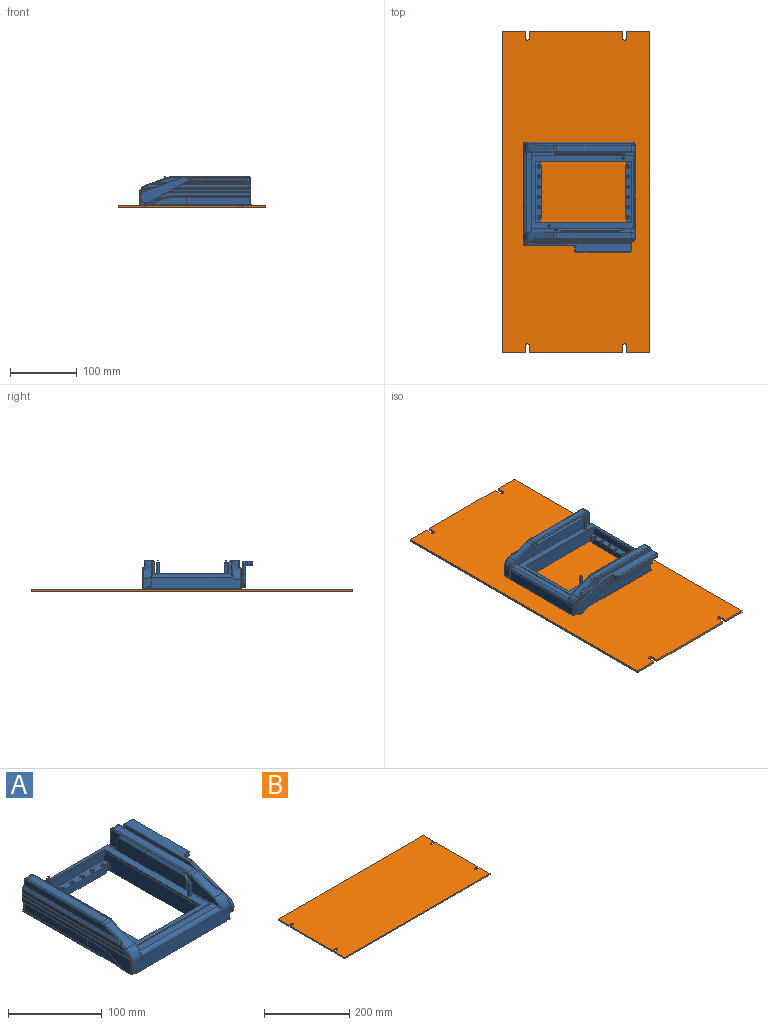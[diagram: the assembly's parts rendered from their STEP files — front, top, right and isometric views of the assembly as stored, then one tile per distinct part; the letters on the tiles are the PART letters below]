
ASSEMBLY  parts=2 mates=1
PART A: 333 faces, bbox 167.3x170.3x45.8 mm
  f0: plane 100.6x2.54mm, normal (0.71,0,0.71), area 346.7mm2, adj f1,f2,f3,f7
  f1: cylinder r=9.65mm len=9.65mm, axis (-1,0,0), area 36.1mm2, adj f0,f3,f4,f6,f7
  f2: cylinder r=9.65mm len=9.65mm, axis (1,0,0), area 36.1mm2, adj f0,f3,f5,f6,f7
  f3: plane 87.55x0.64mm, normal (0,0,1), area 55.6mm2, adj f0,f1,f2,f6
  f4: plane 11.86x3.18mm, normal (0,-1,0), area 37.7mm2, adj f1,f6,f7,f8
  f5: plane 11.86x3.18mm, normal (0,1,0), area 37.7mm2, adj f2,f6,f7,f8
  f6: plane 106.85x21.51mm, normal (-1,0,0), area 2258.8mm2, adj f1,f2,f3,f4,f5,f8
  f7: plane 106.85x18.97mm, normal (1,0,0), area 2013.7mm2, adj f0,f1,f2,f4,f5,f8
  f8: plane 154.94x122.53mm, normal (0,0,1), area 856.5mm2, adj f4,f5,f6,f7,f9,f10,f11,f12
  f9: plane 106.85x18.97mm, normal (-1,0,0), area 2013.7mm2, adj f8,f10,f12,f24,f25,f26
  f10: plane 11.86x3.18mm, normal (0,1,0), area 37.7mm2, adj f8,f9,f11,f26
  f11: plane 106.85x21.51mm, normal (1,0,0), area 2258.8mm2, adj f8,f10,f12,f24,f26,f27
  f12: plane 11.86x3.18mm, normal (0,-1,0), area 37.7mm2, adj f8,f9,f11,f24
  f13: plane 109.73x2.36mm, normal (0,-1,0), area 259.2mm2, adj f8,f14,f16,f28
  f14: plane 153.16x2.36mm, normal (-1,0,0), area 361.8mm2, adj f8,f13,f15,f28
  f15: plane 109.73x2.36mm, normal (0,1,0), area 259.2mm2, adj f8,f14,f16,f28
  f16: plane 153.16x2.36mm, normal (1,0,0), area 361.8mm2, adj f8,f13,f15,f28
  f17: plane 162.68x20.83mm, normal (-1,0,0), area 3006.5mm2, adj f8,f18,f23,f29,f30,f31,f32,f33
  f18: cylinder r=1.52mm len=17.53mm, axis (0,0,-1), area 38.5mm2, adj f8,f17,f34,f36,f37,f38,f39,f45
  f19: plane 167.66x18.05mm, normal (-1,0,0), area 53.8mm2, adj f8,f20,f43,f45,f46,f47,f48,f49
  f20: cylinder r=0.51mm len=12.68mm, axis (1,0.03,0), area 9.3mm2, adj f8,f19,f21,f51,f52,f53
  f21: cylinder r=1.52mm len=17.86mm, axis (0,0,-1), area 41.1mm2, adj f8,f20,f22,f53,f54,f55,f56,f57
  f22: plane 162.82x21.1mm, normal (1,0,0), area 3049.8mm2, adj f8,f21,f23,f29,f35,f60,f61,f62
  f23: plane 118.36x1.27mm, normal (0,1,0), area 150.3mm2, adj f8,f17,f22,f35
  f24: cylinder r=9.65mm len=9.65mm, axis (-1,0,0), area 36.1mm2, adj f9,f11,f12,f25,f27
  f25: plane 100.6x2.54mm, normal (-0.71,0,0.71), area 346.7mm2, adj f9,f24,f26,f27
  f26: cylinder r=9.65mm len=9.65mm, axis (1,0,0), area 36.1mm2, adj f9,f10,f11,f25,f27
  f27: plane 87.55x0.64mm, normal (0,0,1), area 55.6mm2, adj f11,f24,f25,f26
  f28: plane 153.16x109.73mm, normal (0,0,1), area 3395.6mm2, adj f13,f14,f15,f16,f64,f65,f66,f67
  f29: cylinder r=4.83mm len=123.65mm, axis (-1,0,0), area 914.9mm2, adj f17,f22,f30,f35,f63,f68,f69,f70
  f30: torus R=14.35mm, axis (-1,0,0), area 28.9mm2, adj f17,f29,f31,f69
  f31: cylinder r=1.52mm len=35.07mm, axis (0,-0.94,-0.34), area 88mm2, adj f17,f30,f32,f72
  f32: torus R=14.35mm, axis (-1,0,0), area 12.8mm2, adj f17,f31,f33,f73
  f33: cylinder r=1.52mm len=112.51mm, axis (0,1,0), area 269.2mm2, adj f17,f32,f34,f74
  f34: torus R=3.3mm, axis (-1,0,0), area 16mm2, adj f17,f18,f33,f75
  f35: plane 118.36x7.87mm, normal (0,0,1), area 932mm2, adj f17,f22,f23,f29
  f36: plane 12.45x12.07mm, normal (0,1,0), area 125.9mm2, adj f18,f75,f76,f77,f78,f79,f80
  f37: torus R=1.02mm, axis (0,0,-1), area 1mm2, adj f18,f38,f80,f81
  f38: plane 12.87x2.4mm, normal (0,1,0), area 14.6mm2, adj f18,f37,f39,f81,f82,f83
  f39: torus R=1.02mm, axis (0,0,-1), area 1mm2, adj f18,f38,f83,f84
  f40: plane 167.64x0.25mm, normal (1,0,0), area 9.7mm2, adj f41,f45,f87,f88,f89,f105
  f41: plane 165.1x142.24mm, normal (0,0,1), area 1026.7mm2, adj f40,f42,f45,f88,f90,f91,f92
  f42: plane 167.64x2.54mm, normal (-1,0,0), area 66.3mm2, adj f41,f43,f45,f47,f87,f88,f93,f94
  f43: plane 167.64x6.5mm, normal (0,0,1), area 1089.7mm2, adj f19,f42,f45,f95,f105
  f44: plane 2.16x0.76mm, normal (1,0,0), area 1mm2, adj f45,f86,f96,f97,f98,f99
  f45: plane 141.1x23.3mm, normal (0,1,0), area 2728.3mm2, adj f8,f18,f19,f40,f41,f42,f43,f44
  f46: plane 167.49x8.28mm, normal (0.02,0,-1), area 1087.4mm2, adj f19,f47,f93,f95,f104,f105
  f47: plane 18.26x11.1mm, normal (-0.03,1,0), area 145mm2, adj f19,f42,f46,f48,f94,f95,f106,f107
  f48: cylinder r=0.51mm len=11.02mm, axis (-1,-0.03,0), area 8.8mm2, adj f19,f47,f49,f109
  f49: plane 11.64x0.66mm, normal (0,0,1), area 2.9mm2, adj f19,f48,f50,f109
  f50: plane 11.71x1.15mm, normal (-0.03,1,0), area 13.4mm2, adj f19,f49,f51,f52,f109,f110
  f51: plane 11.64x0.66mm, normal (0,0,-1), area 2.9mm2, adj f19,f20,f50,f52
  f52: torus R=1.02mm, axis (0,0,-1), area 1.6mm2, adj f20,f50,f51,f110,f111,f112,f113
  f53: plane 12.07x2.92mm, normal (-0.03,1,0), area 35.3mm2, adj f20,f21,f54,f112
  f54: cylinder r=0.51mm len=13.22mm, axis (-1,-0.03,0), area 10.1mm2, adj f21,f53,f55,f114
  f55: plane 14.06x0.74mm, normal (0,0,1), area 3.5mm2, adj f21,f54,f56,f114
  f56: plane 14.12x1.15mm, normal (-0.03,1,0), area 16.1mm2, adj f21,f55,f57,f114,f115,f116
  f57: plane 14.06x0.74mm, normal (0,0,-1), area 3.5mm2, adj f21,f56,f58,f116
  f58: cylinder r=0.51mm len=13.22mm, axis (1,0.03,0), area 10.1mm2, adj f21,f57,f59,f116
  f59: plane 12.54x12.16mm, normal (-0.03,1,0), area 126mm2, adj f21,f58,f117,f118,f119,f120,f121
  f60: torus R=3.25mm, axis (1,0,0), area 16.3mm2, adj f21,f22,f117,f332
  f61: torus R=14.3mm, axis (1,0,0), area 13.1mm2, adj f22,f62,f123,f332
  f62: cylinder r=1.52mm len=35.07mm, axis (0,0.94,0.34), area 90mm2, adj f22,f61,f63,f124
  f63: torus R=14.3mm, axis (1,0,0), area 32mm2, adj f22,f29,f62,f70
  f64: plane 92.46x2.36mm, normal (0,-1,0), area 218.4mm2, adj f28,f65,f67,f125
  f65: plane 144.78x2.36mm, normal (-1,0,0), area 342mm2, adj f28,f64,f66,f125
  f66: plane 92.46x2.36mm, normal (0,1,0), area 218.4mm2, adj f28,f65,f67,f125
  f67: plane 144.78x2.36mm, normal (1,0,0), area 342mm2, adj f28,f64,f66,f125
  f68: plane 5.42x0.96mm, normal (1,0,0), area 0.8mm2, adj f29,f69,f105
  f69: cylinder r=15.88mm len=14.92mm, axis (-1,0,0), area 227.8mm2, adj f29,f30,f68,f72,f105,f126
  f70: cone r=15.88mm half-angle=2deg, axis (1,0,0), area 227.8mm2, adj f29,f63,f71,f93,f103,f105,f124,f127
  f71: plane 2.49x0.5mm, normal (-1,0,0), area 0.2mm2, adj f29,f70,f105
  f72: plane 34.82x12.85mm, normal (0,-0.34,0.94), area 350.2mm2, adj f31,f69,f73,f128,f129,f130,f131
  f73: cylinder r=15.88mm len=8.89mm, axis (-1,0,0), area 49.3mm2, adj f32,f72,f74,f132
  f74: plane 112.39x8.89mm, normal (0,0,1), area 999.1mm2, adj f33,f73,f75,f133
  f75: cylinder r=4.83mm len=8.89mm, axis (-1,0,0), area 67.4mm2, adj f34,f36,f74,f134
  f76: cylinder r=1.52mm len=5.21mm, axis (0,0,-1), area 12.5mm2, adj f36,f77,f134,f135
  f77: torus R=3.05mm, axis (0,1,0), area 7.8mm2, adj f36,f76,f78,f136
  f78: cylinder r=1.52mm len=1.52mm, axis (1,0,0), area 0.3mm2, adj f36,f77,f137,f138
  f79: cylinder r=1.52mm len=4.19mm, axis (0,0,-1), area 10mm2, adj f36,f137,f139,f140
  f80: cylinder r=0.51mm len=12.07mm, axis (-1,0,0), area 9.6mm2, adj f36,f37,f81,f140
  f81: plane 154.7x13.75mm, normal (0,0,-1), area 41.9mm2, adj f37,f38,f80,f82,f140,f141,f142,f143
  f82: cylinder r=1.52mm len=1.52mm, axis (0,0,1), area 2.7mm2, adj f38,f81,f83,f143
  f83: plane 154.7x13.75mm, normal (0,0,1), area 41.9mm2, adj f38,f39,f82,f84,f142,f143,f144,f145
  f84: cylinder r=0.51mm len=12.07mm, axis (1,0,0), area 9.6mm2, adj f39,f45,f83,f144
  f85: cylinder r=1.52mm len=2.92mm, axis (0,0,-1), area 7mm2, adj f45,f144,f146,f147
  f86: cylinder r=0.51mm len=10.95mm, axis (-1,0,0), area 8.7mm2, adj f44,f45,f96,f147
  f87: plane 136.65x3.3mm, normal (0,0,-1), area 451.2mm2, adj f40,f42,f88,f105
  f88: plane 142.24x1.8mm, normal (0,-1,0), area 228.7mm2, adj f40,f41,f42,f87,f90,f92,f148
  f89: plane 167.67x6mm, normal (0,0,-1), area 590.9mm2, adj f40,f45,f102,f105,f149,f150,f151,f152
  f90: plane 165.1x1.8mm, normal (1,0,0), area 297.2mm2, adj f41,f88,f91,f148
  f91: plane 142.24x1.8mm, normal (0,1,0), area 256.1mm2, adj f41,f90,f92,f148
  f92: plane 165.1x1.8mm, normal (-1,0,0), area 297.2mm2, adj f41,f88,f91,f148
  f93: plane 14.22x12.07mm, normal (-0.03,-1,0), area 155.1mm2, adj f42,f46,f70,f94,f95,f104,f155
  f94: plane 167.04x6mm, normal (0,0,-1), area 587.4mm2, adj f42,f47,f93,f106,f155,f156,f157,f158
  f95: plane 167x0.17mm, normal (1,0,0), area 28.5mm2, adj f43,f46,f47,f93
  f96: plane 157.24x11.96mm, normal (0,0,-1), area 42.1mm2, adj f44,f86,f97,f147,f161,f162,f163,f164
  f97: plane 10.18x1.14mm, normal (0,1,0), area 11.6mm2, adj f44,f96,f98,f164
  f98: plane 154.34x11.96mm, normal (0,0,1), area 42mm2, adj f44,f97,f99,f162,f163,f164,f165,f166
  f99: cylinder r=0.51mm len=10.95mm, axis (1,0,0), area 8.7mm2, adj f44,f45,f98,f166
  f100: cylinder r=1.52mm len=4.19mm, axis (0,0,-1), area 10mm2, adj f45,f149,f166,f167
  f101: torus R=3.05mm, axis (0,1,0), area 7.8mm2, adj f45,f102,f167,f168
  f102: cylinder r=1.52mm len=10.92mm, axis (0,0,-1), area 26.1mm2, adj f45,f89,f101,f151
  f103: torus R=14.3mm, axis (1,0,0), area 0.8mm2, adj f70,f104,f105
  f104: cylinder r=1.52mm len=11.96mm, axis (0,0,-1), area 8.8mm2, adj f46,f93,f103,f105
  f105: plane 141.72x17.64mm, normal (0,-1,0), area 2253.4mm2, adj f19,f29,f40,f42,f43,f46,f68,f69
  f106: cylinder r=1.52mm len=10.92mm, axis (0,0,-1), area 25.6mm2, adj f47,f94,f107,f160
  f107: bspline ~3.05x3.05mm, area 7.7mm2, adj f47,f106,f169,f170
  f108: cylinder r=1.52mm len=4.19mm, axis (0,0,-1), area 9.8mm2, adj f47,f109,f156,f169
  f109: torus R=1.02mm, axis (0,0,-1), area 1.6mm2, adj f48,f49,f50,f108,f110,f171,f172
  f110: plane 143.84x1.15mm, normal (-1,0,0), area 164.4mm2, adj f50,f52,f109,f113,f172,f173
  f111: cylinder r=0.51mm len=162.23mm, axis (0,-1,0), area 128.4mm2, adj f52,f113,f173,f174,f175
  f112: cylinder r=1.52mm len=2.92mm, axis (0,0,-1), area 6.8mm2, adj f52,f53,f114,f175
  f113: plane 156.42x0.25mm, normal (0,0,-1), area 38.6mm2, adj f52,f110,f111,f173
  f114: torus R=1.02mm, axis (0,0,-1), area 1.6mm2, adj f54,f55,f56,f112,f115,f176,f177
  f115: plane 141.3x1.15mm, normal (-1,0,0), area 161.5mm2, adj f56,f114,f116,f177,f178,f179
  f116: torus R=1.02mm, axis (0,0,-1), area 1.6mm2, adj f56,f57,f58,f115,f118,f178,f180
  f117: cone r=4.83mm half-angle=2deg, axis (1,0,0), area 64.5mm2, adj f59,f60,f122,f181
  f118: cylinder r=1.52mm len=4.19mm, axis (0,0,-1), area 9.8mm2, adj f59,f116,f182,f183
  f119: cylinder r=1.52mm len=1.53mm, axis (-1,-0.03,0), area 0.3mm2, adj f59,f120,f183,f184
  f120: bspline ~3.05x3.05mm, area 7.7mm2, adj f59,f119,f121,f185
  f121: cylinder r=1.52mm len=5.21mm, axis (0,0,-1), area 12.2mm2, adj f59,f120,f181,f186
  f122: plane 112.39x8.89mm, normal (-0.03,0,1), area 999.8mm2, adj f117,f123,f187,f332
  f123: cone r=15.88mm half-angle=2deg, axis (1,0,0), area 48.6mm2, adj f61,f122,f124,f188
  f124: plane 34.92x13.24mm, normal (-0.03,-0.34,0.94), area 354mm2, adj f62,f70,f123,f189,f190,f191,f192
  f125: plane 144.78x92.46mm, normal (0,0,1), area 120.3mm2, adj f64,f65,f66,f67,f194,f195,f196,f197
  f126: torus R=14.35mm, axis (1,0,0), area 42.1mm2, adj f69,f128,f139,f142,f146,f149,f150,f162
  f127: torus R=13.88mm, axis (-1,0,0), area 39.3mm2, adj f70,f155,f156,f173,f174,f175,f179,f182
  f128: cylinder r=1.52mm len=5.7mm, axis (0,-0.94,-0.34), area 13.2mm2, adj f72,f126,f139,f206
  f129: cylinder r=1.52mm len=0.52mm, axis (-1,0,0), area 0.1mm2, adj f72,f130,f138,f206
  f130: bspline ~8.9x3.05mm, area 14.3mm2, adj f72,f129,f131,f136
  f131: cylinder r=1.52mm len=21.52mm, axis (0,0.94,0.34), area 53.5mm2, adj f72,f130,f132,f135
  f132: torus R=14.35mm, axis (1,0,0), area 12.8mm2, adj f73,f131,f133,f135
  f133: cylinder r=1.52mm len=112.39mm, axis (0,1,0), area 269mm2, adj f74,f132,f134,f135
  f134: torus R=3.3mm, axis (1,0,0), area 16.1mm2, adj f75,f76,f133,f135
  f135: plane 141.6x8.51mm, normal (1,0,0), area 1102.7mm2, adj f76,f131,f132,f133,f134,f136
  f136: cylinder r=1.52mm len=149.98mm, axis (0,1,0), area 351.7mm2, adj f77,f130,f135,f138
  f137: sphere r=1.52mm, area 2.3mm2, adj f78,f79,f207
  f138: plane 149.98x0.13mm, normal (0,0,1), area 19mm2, adj f78,f129,f136,f207
  f139: plane 159.34x4.27mm, normal (1,0,0), area 650.8mm2, adj f79,f126,f128,f141,f202,f207
  f140: torus R=1.02mm, axis (0,0,-1), area 1.7mm2, adj f79,f80,f81,f141
  f141: cylinder r=0.51mm len=153.69mm, axis (0,-1,0), area 122.6mm2, adj f81,f139,f140,f202
  f142: cylinder r=315.21mm len=20.88mm, axis (0,0,1), area 23.6mm2, adj f81,f83,f126,f143,f145,f199,f202
  f143: plane 140.27x1.14mm, normal (1,0,0), area 160.3mm2, adj f81,f82,f83,f142
  f144: torus R=1.02mm, axis (0,0,-1), area 1.7mm2, adj f83,f84,f85,f145
  f145: cylinder r=0.51mm len=161.4mm, axis (0,1,0), area 127.3mm2, adj f83,f142,f144,f146,f199
  f146: plane 163.23x2.92mm, normal (1,0,0), area 474.4mm2, adj f85,f126,f145,f161
  f147: torus R=1.02mm, axis (0,0,-1), area 1.7mm2, adj f85,f86,f96,f161
  f148: plane 165.1x142.24mm, normal (0,0,-1), area 9069.4mm2, adj f88,f90,f91,f92,f208,f209,f210,f211
  f149: plane 164.6x18.17mm, normal (1,0,0), area 886.7mm2, adj f89,f100,f126,f150,f154,f165,f216,f217
  f150: cylinder r=1.52mm len=14.22mm, axis (0,0,1), area 34mm2, adj f89,f105,f126,f149
  f151: plane 95.57x10.92mm, normal (1,0,0), area 1043.8mm2, adj f89,f102,f152,f168
  f152: cylinder r=508mm len=52.87mm, axis (0,0,-1), area 365mm2, adj f89,f151,f153,f219
  f153: bspline ~40.64x12.99mm, area 59.1mm2, adj f89,f152,f154,f219
  f154: bspline ~40.94x14.48mm, area 72.9mm2, adj f89,f149,f153,f217
  f155: cylinder r=1.52mm len=14.22mm, axis (0,0,1), area 33.3mm2, adj f93,f94,f127,f156
  f156: plane 163.65x18.17mm, normal (-1,0,0), area 1051.1mm2, adj f94,f108,f127,f155,f157,f171,f220,f221
  f157: bspline ~40.94x14.48mm, area 72.9mm2, adj f94,f156,f158,f221
  f158: bspline ~40.64x12.99mm, area 69.9mm2, adj f94,f157,f159,f222
  f159: cylinder r=508mm len=52.87mm, axis (0,0,-1), area 365mm2, adj f94,f158,f160,f222
  f160: plane 95.2x10.92mm, normal (-1,0,0), area 1039.7mm2, adj f94,f106,f159,f170
  f161: cylinder r=0.51mm len=163.23mm, axis (0,-1,0), area 128.9mm2, adj f96,f146,f147,f162,f201
  f162: cylinder r=315.21mm len=20.92mm, axis (0,0,1), area 24.2mm2, adj f96,f98,f126,f161,f163,f200,f201,f216
  f163: plane 142.81x1.14mm, normal (1,0,0), area 163.2mm2, adj f96,f98,f162,f164
  f164: cylinder r=1.52mm len=1.52mm, axis (0,0,1), area 2.7mm2, adj f96,f97,f98,f163
  f165: cylinder r=0.51mm len=153.33mm, axis (0,1,0), area 121.8mm2, adj f98,f149,f166,f327
  f166: torus R=1.02mm, axis (0,0,-1), area 1.7mm2, adj f98,f99,f100,f165
  f167: sphere r=1.52mm, area 2.3mm2, adj f100,f101,f218
  f168: cylinder r=1.52mm len=95.57mm, axis (0,1,0), area 228.8mm2, adj f101,f151,f218,f219
  f169: sphere r=1.52mm, area 2.3mm2, adj f107,f108,f220
  f170: cylinder r=1.52mm len=95.2mm, axis (0,1,0), area 227.8mm2, adj f107,f160,f220,f222
  f171: cylinder r=0.51mm len=163.07mm, axis (0,1,0), area 128.8mm2, adj f109,f156,f172,f173,f204
  f172: plane 156.42x0.25mm, normal (0,0,1), area 38.6mm2, adj f109,f110,f171,f173
  f173: cylinder r=315.21mm len=20.51mm, axis (0,0,1), area 24.2mm2, adj f110,f111,f113,f127,f171,f172,f174,f204
  f174: bspline ~0.67x0.48mm, area 0.2mm2, adj f111,f127,f173
  f175: plane 162.23x2.92mm, normal (-1,0,0), area 471.3mm2, adj f111,f112,f127,f176
  f176: cylinder r=0.51mm len=160.31mm, axis (0,1,0), area 126.5mm2, adj f114,f175,f177,f179,f205
  f177: plane 153.88x0.25mm, normal (0,0,1), area 38mm2, adj f114,f115,f176,f179
  f178: plane 153.88x0.25mm, normal (0,0,-1), area 38mm2, adj f115,f116,f179,f180
  f179: cylinder r=315.21mm len=20.37mm, axis (0,0,1), area 23.1mm2, adj f115,f127,f176,f177,f178,f203,f205
  f180: cylinder r=0.51mm len=153.21mm, axis (0,-1,0), area 122.3mm2, adj f116,f178,f182,f203
  f181: torus R=2.94mm, axis (-1,0,0), area 14.3mm2, adj f117,f121,f186,f187
  f182: plane 158.06x4.25mm, normal (-1,0,0), area 643.8mm2, adj f118,f127,f180,f192,f203,f223
  f183: sphere r=1.52mm, area 3.6mm2, adj f118,f119,f223
  f184: plane 148.13x0.13mm, normal (0,0,1), area 18.8mm2, adj f119,f185,f191,f223
  f185: cylinder r=1.52mm len=148.24mm, axis (0,1,0), area 347.9mm2, adj f120,f184,f186,f190
  f186: plane 140.17x8.14mm, normal (-1,0,0), area 1048.3mm2, adj f121,f181,f185,f187,f188,f189
  f187: cylinder r=1.52mm len=112.39mm, axis (0,1,0), area 263.1mm2, adj f122,f181,f186,f188
  f188: torus R=13.99mm, axis (-1,0,0), area 12.2mm2, adj f123,f186,f187,f189
  f189: cylinder r=1.52mm len=20.58mm, axis (0,-0.94,-0.34), area 50mm2, adj f124,f186,f188,f190
  f190: bspline ~8.62x3.05mm, area 13.6mm2, adj f124,f185,f189,f191
  f191: cylinder r=1.52mm len=0.53mm, axis (-0.99,0.1,0), area 0.1mm2, adj f124,f184,f190,f224
  f192: cylinder r=1.52mm len=6.92mm, axis (0,0.94,0.34), area 15.9mm2, adj f124,f127,f182,f224
  f193: plane 1.66x1.66mm, normal (0,0,1), area 2.2mm2, adj f329
  f194: plane 144.27x20.57mm, normal (1,0,0), area 2779.5mm2, adj f125,f195,f197,f225,f226,f227,f228,f320
  f195: plane 91.95x11.05mm, normal (0,-1,0), area 1015.9mm2, adj f125,f194,f196,f228
  f196: plane 144.27x20.57mm, normal (-1,0,0), area 2779.5mm2, adj f125,f195,f197,f225,f226,f228,f229,f319
  f197: plane 91.95x11.05mm, normal (0,1,0), area 1015.9mm2, adj f125,f194,f196,f225
  f198: plane 1.66x1.66mm, normal (0,0,1), area 2.2mm2, adj f328
  f199: bspline ~0.51x0.35mm, area 0.1mm2, adj f126,f142,f145
  f200: bspline ~0.46x0.32mm, area 0.1mm2, adj f126,f162,f216
  f201: bspline ~0.62x0.44mm, area 0.1mm2, adj f126,f161,f162
  f202: bspline ~7.16x0.51mm, area 4.1mm2, adj f126,f139,f141,f142
  f203: bspline ~6.57x0.51mm, area 3.8mm2, adj f127,f179,f180,f182
  f204: bspline ~0.54x0.36mm, area 0.1mm2, adj f127,f171,f173
  f205: bspline ~0.62x0.4mm, area 0.1mm2, adj f127,f176,f179
  f206: sphere r=1.52mm, area 0.6mm2, adj f128,f129,f207
  f207: cylinder r=1.52mm len=149.98mm, axis (0,-1,0), area 359mm2, adj f137,f138,f139,f206
  f208: cylinder r=6.35mm len=6.35mm, axis (0,0,1), area 16mm2, adj f148,f209,f215,f226
  f209: plane 84.33x1.6mm, normal (0,-1,0), area 134.9mm2, adj f148,f208,f210,f226
  f210: cylinder r=6.35mm len=6.35mm, axis (0,0,1), area 16mm2, adj f148,f209,f211,f226
  f211: plane 135.38x1.6mm, normal (1,0,0), area 216.6mm2, adj f148,f210,f212,f226
  f212: cylinder r=6.35mm len=6.35mm, axis (0,0,1), area 16mm2, adj f148,f211,f213,f226
  f213: plane 84.33x1.6mm, normal (0,1,0), area 134.9mm2, adj f148,f212,f214,f226
  f214: cylinder r=6.35mm len=6.35mm, axis (0,0,1), area 16mm2, adj f148,f213,f215,f226
  f215: plane 135.38x1.6mm, normal (-1,0,0), area 216.6mm2, adj f148,f208,f214,f226
  f216: cylinder r=0.51mm len=6.46mm, axis (0,1,0), area 3.1mm2, adj f149,f162,f200,f327
  f217: bspline ~13.83x1.53mm, area 32.7mm2, adj f149,f154,f218,f219
  f218: cylinder r=1.52mm len=95.57mm, axis (0,1,0), area 228.8mm2, adj f149,f167,f168,f217
  f219: torus R=506.48mm, axis (0,0,1), area 32.5mm2, adj f152,f153,f168,f217
  f220: cylinder r=1.52mm len=95.09mm, axis (0,1,0), area 227.6mm2, adj f156,f169,f170,f221
  f221: bspline ~13.83x1.53mm, area 32.7mm2, adj f156,f157,f220,f222
  f222: torus R=506.48mm, axis (0,0,1), area 32.5mm2, adj f158,f159,f170,f221
  f223: cylinder r=1.52mm len=148.11mm, axis (0,-1,0), area 354.6mm2, adj f182,f183,f184,f224
  f224: sphere r=1.52mm, area 0.6mm2, adj f191,f192,f223
  f225: plane 91.95x9.91mm, normal (0,0,1), area 675.2mm2, adj f194,f196,f197,f236,f313,f314,f315,f316
  f226: plane 148.08x97.03mm, normal (0,0,-1), area 2620.8mm2, adj f194,f196,f208,f209,f210,f211,f212,f213
  f227: cylinder r=3.05mm len=9.53mm, axis (0,0,1), area 81.3mm2, adj f194,f226,f228,f237
  f228: plane 91.95x9.91mm, normal (0,0,1), area 675.2mm2, adj f194,f195,f196,f227,f229,f237,f295,f296
  f229: cylinder r=3.05mm len=9.53mm, axis (0,0,1), area 81.3mm2, adj f196,f226,f228,f237
  f230: plane 4.32x4.32mm, normal (0,0,-1), area 14.6mm2, adj f326
  f231: plane 4.32x4.32mm, normal (0,0,-1), area 14.6mm2, adj f325
  f232: plane 5.33x5.33mm, normal (0,0,-1), area 8.6mm2, adj f238,f294,f324
  f233: plane 4.32x4.32mm, normal (0,0,-1), area 14.6mm2, adj f323
  f234: plane 4.32x4.32mm, normal (0,0,-1), area 14.6mm2, adj f322
  f235: plane 160.53x37.8mm, normal (-1,0,0), area 1187.7mm2, adj f239,f240,f241,f242,f243,f244,f293,f321
  f236: plane 80.1x9.53mm, normal (0,1,0), area 763mm2, adj f225,f226,f319,f320
  f237: plane 80.1x9.53mm, normal (0,-1,0), area 763mm2, adj f226,f227,f228,f229
  f238: plane 4.3x2.54mm, normal (1,0,0), area 10.9mm2, adj f232,f257,f294
  f239: cylinder r=0.76mm len=56.73mm, axis (0,-0.94,-0.34), area 71.9mm2, adj f235,f258,f259,f293
  f240: cylinder r=0.76mm len=98.21mm, axis (0,1,0), area 117.6mm2, adj f235,f259,f260,f261
  f241: cylinder r=0.76mm len=4.83mm, axis (0,0,1), area 5.8mm2, adj f235,f260,f262,f263
  f242: cylinder r=0.76mm len=88.14mm, axis (0,1,0), area 105.5mm2, adj f235,f243,f263,f264
  f243: torus R=7.11mm, axis (-1,0,0), area 4mm2, adj f235,f242,f244,f265
  f244: cylinder r=0.76mm len=56.1mm, axis (0,0.87,0.49), area 76.3mm2, adj f235,f243,f266,f293
  f245: plane 5.16x5.16mm, normal (0,0,1), area 16.9mm2, adj f307,f318
  f246: plane 5.16x5.16mm, normal (0,0,1), area 16.9mm2, adj f308,f317
  f247: plane 5.16x5.16mm, normal (0,0,1), area 16.9mm2, adj f309,f316
  f248: plane 5.16x5.16mm, normal (0,0,1), area 16.9mm2, adj f310,f315
  f249: plane 5.16x5.16mm, normal (0,0,1), area 16.9mm2, adj f311,f314
  f250: plane 5.16x5.16mm, normal (0,0,1), area 16.9mm2, adj f312,f313
  f251: plane 5.16x5.16mm, normal (0,0,1), area 16.9mm2, adj f295,f306
  f252: plane 5.16x5.16mm, normal (0,0,1), area 16.9mm2, adj f296,f305
  f253: plane 5.16x5.16mm, normal (0,0,1), area 16.9mm2, adj f297,f304
  f254: plane 5.16x5.16mm, normal (0,0,1), area 16.9mm2, adj f298,f303
  f255: plane 5.16x5.16mm, normal (0,0,1), area 16.9mm2, adj f299,f302
  f256: plane 5.16x5.16mm, normal (0,0,1), area 16.9mm2, adj f300,f301
  f257: plane 4.78x3.43mm, normal (0,0,-1), area 13.8mm2, adj f238,f294
  f258: plane 56.46x20.55mm, normal (0,-0.34,0.94), area 193.8mm2, adj f239,f267,f268,f269
  f259: sphere r=0.76mm, area 0.2mm2, adj f239,f240,f269
  f260: sphere r=0.76mm, area 0.9mm2, adj f240,f241,f270
  f261: plane 98.21x12.62mm, normal (0,0,1), area 1110.8mm2, adj f240,f269,f270,f271,f272,f273,f274,f275
  f262: plane 10.97x4.83mm, normal (0,1,0), area 53mm2, adj f241,f270,f277,f278
  f263: sphere r=0.76mm, area 0.6mm2, adj f241,f242,f278
  f264: plane 88.14x13.39mm, normal (0,0,-1), area 1140.6mm2, adj f242,f265,f278,f279,f280,f281,f282,f283
  f265: cylinder r=6.35mm len=3.23mm, axis (1,0,0), area 10.4mm2, adj f243,f264,f266,f284
  f266: plane 55.73x30.96mm, normal (0,0.49,-0.87), area 205.6mm2, adj f244,f265,f267,f285
  f267: cylinder r=9.65mm len=18.72mm, axis (1,0,0), area 102.7mm2, adj f258,f266,f292,f293
  f268: cylinder r=0.76mm len=56.73mm, axis (0,0.94,0.34), area 71.9mm2, adj f258,f286,f287,f292
  f269: cylinder r=0.76mm len=3.23mm, axis (-1,0,0), area 0.9mm2, adj f258,f259,f261,f287
  f270: cylinder r=0.76mm len=10.97mm, axis (1,0,0), area 13.1mm2, adj f260,f261,f262,f274
  f271: cylinder r=0.76mm len=3.81mm, axis (-1,0,0), area 4.6mm2, adj f261,f272,f276,f288
  f272: torus R=2.41mm, axis (0,0,-1), area 2.5mm2, adj f261,f271,f273,f289
  f273: plane 84.38x1.89mm, normal (0.71,0,0.71), area 178.9mm2, adj f261,f272,f274,f277,f289,f290
  f274: torus R=2.41mm, axis (0,0,-1), area 2.5mm2, adj f261,f270,f273,f277
  f275: cylinder r=0.76mm len=10.08mm, axis (0,-1,0), area 12.1mm2, adj f261,f276,f286,f287
  f276: torus R=3.94mm, axis (0,0,-1), area 6.5mm2, adj f261,f271,f275,f291
  f277: cylinder r=3.17mm len=4.83mm, axis (0,0,-1), area 23.2mm2, adj f262,f273,f274,f279,f290
  f278: cylinder r=0.76mm len=10.97mm, axis (1,0,0), area 13.1mm2, adj f262,f263,f264,f279
  f279: torus R=2.41mm, axis (0,0,-1), area 5.4mm2, adj f264,f277,f278,f280
  f280: cylinder r=0.76mm len=79.38mm, axis (0,-1,0), area 95mm2, adj f264,f279,f281,f290
  f281: torus R=2.41mm, axis (0,0,-1), area 5.4mm2, adj f264,f280,f282,f289
  f282: cylinder r=0.76mm len=3.81mm, axis (1,0,0), area 4.6mm2, adj f264,f281,f283,f288
  f283: torus R=3.94mm, axis (0,0,-1), area 6.5mm2, adj f264,f282,f284,f291
  f284: torus R=7.11mm, axis (-1,0,0), area 4mm2, adj f265,f283,f285,f286
  f285: cylinder r=0.76mm len=56.1mm, axis (0,-0.87,-0.49), area 76.3mm2, adj f266,f284,f286,f292
  f286: plane 72.39x37.8mm, normal (1,0,0), area 966mm2, adj f268,f275,f284,f285,f291,f292
  f287: sphere r=0.76mm, area 0.2mm2, adj f268,f269,f275
  f288: plane 4.83x3.81mm, normal (0,-1,0), area 18.4mm2, adj f271,f282,f289,f291
  f289: cylinder r=3.17mm len=4.83mm, axis (0,0,-1), area 23.2mm2, adj f272,f273,f281,f288,f290
  f290: plane 79.38x4.06mm, normal (1,0,0), area 322.6mm2, adj f273,f277,f280,f289
  f291: cylinder r=3.17mm len=4.83mm, axis (0,0,1), area 24.1mm2, adj f276,f283,f286,f288
  f292: torus R=8.89mm, axis (-1,0,0), area 37mm2, adj f267,f268,f285,f286
  f293: torus R=8.89mm, axis (-1,0,0), area 37mm2, adj f235,f239,f244,f267
  f294: cylinder r=2.39mm len=4.78mm, axis (0,0,-1), area 24.5mm2, adj f232,f238,f257
  f295: cylinder r=2.58mm len=5.16mm, axis (0,0,1), area 49.4mm2, adj f228,f251
  f296: cylinder r=2.58mm len=5.16mm, axis (0,0,1), area 49.4mm2, adj f228,f252
  f297: cylinder r=2.58mm len=5.16mm, axis (0,0,1), area 49.4mm2, adj f228,f253
  f298: cylinder r=2.58mm len=5.16mm, axis (0,0,1), area 49.4mm2, adj f228,f254
  f299: cylinder r=2.58mm len=5.16mm, axis (0,0,1), area 49.4mm2, adj f228,f255
  f300: cylinder r=2.58mm len=5.16mm, axis (0,0,1), area 49.4mm2, adj f228,f256
  f301: cylinder r=1.13mm len=6.48mm, axis (0,0,1), area 46mm2, adj f226,f256
  f302: cylinder r=1.13mm len=6.48mm, axis (0,0,1), area 46mm2, adj f226,f255
  f303: cylinder r=1.13mm len=6.48mm, axis (0,0,1), area 46mm2, adj f226,f254
  f304: cylinder r=1.13mm len=6.48mm, axis (0,0,1), area 46mm2, adj f226,f253
  f305: cylinder r=1.13mm len=6.48mm, axis (0,0,1), area 46mm2, adj f226,f252
  f306: cylinder r=1.13mm len=6.48mm, axis (0,0,1), area 46mm2, adj f226,f251
  f307: cylinder r=1.13mm len=6.48mm, axis (0,0,1), area 46mm2, adj f226,f245
  f308: cylinder r=1.13mm len=6.48mm, axis (0,0,1), area 46mm2, adj f226,f246
  f309: cylinder r=1.13mm len=6.48mm, axis (0,0,1), area 46mm2, adj f226,f247
  f310: cylinder r=1.13mm len=6.48mm, axis (0,0,1), area 46mm2, adj f226,f248
  f311: cylinder r=1.13mm len=6.48mm, axis (0,0,1), area 46mm2, adj f226,f249
  f312: cylinder r=1.13mm len=6.48mm, axis (0,0,1), area 46mm2, adj f226,f250
  f313: cylinder r=2.58mm len=5.16mm, axis (0,0,1), area 49.4mm2, adj f225,f250
  f314: cylinder r=2.58mm len=5.16mm, axis (0,0,1), area 49.4mm2, adj f225,f249
  f315: cylinder r=2.58mm len=5.16mm, axis (0,0,1), area 49.4mm2, adj f225,f248
  f316: cylinder r=2.58mm len=5.16mm, axis (0,0,1), area 49.4mm2, adj f225,f247
  f317: cylinder r=2.58mm len=5.16mm, axis (0,0,1), area 49.4mm2, adj f225,f246
  f318: cylinder r=2.58mm len=5.16mm, axis (0,0,1), area 49.4mm2, adj f225,f245
  f319: cylinder r=3.05mm len=9.53mm, axis (0,0,1), area 81.3mm2, adj f196,f225,f226,f236
  f320: cylinder r=3.05mm len=9.53mm, axis (0,0,1), area 81.3mm2, adj f194,f225,f226,f236
  f321: torus R=8.05mm, axis (-1,0,0), area 38.7mm2, adj f235,f327
  f322: cylinder r=2.16mm len=4.32mm, axis (0,0,1), area 21.7mm2, adj f148,f234
  f323: cylinder r=2.16mm len=4.32mm, axis (0,0,1), area 21.7mm2, adj f148,f233
  f324: cylinder r=2.67mm len=5.33mm, axis (0,0,1), area 26.8mm2, adj f148,f232
  f325: cylinder r=2.16mm len=4.32mm, axis (0,0,1), area 21.7mm2, adj f148,f231
  f326: cylinder r=2.16mm len=4.32mm, axis (0,0,1), area 21.7mm2, adj f148,f230
  f327: cylinder r=7.54mm len=15.09mm, axis (1,0,0), area 56.8mm2, adj f98,f149,f162,f165,f216,f321
  f328: cone r=1.99mm half-angle=20deg, axis (0,0,-1), area 29.9mm2, adj f198,f330
  f329: cone r=1.99mm half-angle=20deg, axis (0,0,-1), area 29.9mm2, adj f193,f331
  f330: cylinder r=1.99mm len=16.56mm, axis (0,0,-1), area 206.5mm2, adj f28,f328
  f331: cylinder r=1.99mm len=16.56mm, axis (0,0,-1), area 206.5mm2, adj f28,f329
  f332: cylinder r=1.52mm len=112.39mm, axis (0,-1,0), area 275mm2, adj f22,f60,f61,f122
PART B: 22 faces, bbox 482.6x221.4x3.2 mm
  f0: plane 139.7x3.18mm, normal (1,0,0), area 443.5mm2, adj f2,f4,f8,f11
  f1: plane 34.52x3.18mm, normal (-1,0,0), area 109.6mm2, adj f4,f8,f13,f20
  f2: plane 10.32x3.18mm, normal (0,-1,0), area 32.8mm2, adj f0,f3,f4,f8
  f3: cylinder r=3.17mm len=6.35mm, axis (0,0,1), area 31.7mm2, adj f2,f4,f8,f21
  f4: plane 482.6x221.44mm, normal (0,0,-1), area 106540.2mm2, adj f0,f1,f2,f3,f5,f6,f7,f9
  f5: plane 482.6x3.18mm, normal (0,1,0), area 1532.3mm2, adj f4,f6,f7,f8
  f6: plane 34.52x3.18mm, normal (1,0,0), area 109.6mm2, adj f4,f5,f8,f9
  f7: plane 34.52x3.18mm, normal (-1,0,0), area 109.6mm2, adj f4,f5,f8,f17
  f8: plane 482.6x221.44mm, normal (0,0,1), area 106540.2mm2, adj f0,f1,f2,f3,f5,f6,f7,f9
  f9: plane 10.32x3.18mm, normal (0,-1,0), area 32.8mm2, adj f4,f6,f8,f10
  f10: cylinder r=3.17mm len=6.35mm, axis (0,0,1), area 31.7mm2, adj f4,f8,f9,f11
  f11: plane 10.32x3.18mm, normal (0,1,0), area 32.8mm2, adj f0,f4,f8,f10
  f12: plane 34.52x3.18mm, normal (1,0,0), area 109.6mm2, adj f4,f8,f13,f21
  f13: plane 482.6x3.18mm, normal (0,-1,0), area 1532.3mm2, adj f1,f4,f8,f12
  f14: plane 10.32x3.18mm, normal (0,1,0), area 32.8mm2, adj f4,f8,f15,f16
  f15: plane 139.7x3.18mm, normal (-1,0,0), area 443.5mm2, adj f4,f8,f14,f18
  f16: cylinder r=3.17mm len=6.35mm, axis (0,0,1), area 31.7mm2, adj f4,f8,f14,f17
  f17: plane 10.32x3.18mm, normal (0,-1,0), area 32.8mm2, adj f4,f7,f8,f16
  f18: plane 10.32x3.18mm, normal (0,-1,0), area 32.8mm2, adj f4,f8,f15,f19
  f19: cylinder r=3.17mm len=6.35mm, axis (0,0,1), area 31.7mm2, adj f4,f8,f18,f20
  f20: plane 10.32x3.18mm, normal (0,1,0), area 32.8mm2, adj f1,f4,f8,f19
  f21: plane 10.32x3.18mm, normal (0,1,0), area 32.8mm2, adj f3,f4,f8,f12
PLACE A rot(axis=(0,0,-1),90deg) t=(111.11,-93.59,-125.99)mm
PLACE B rot(axis=(0.71,0.71,0),180deg) t=(106.91,-6.37,-98.9)mm
MATE planar A.f148 <-> B.f4  axis (0,0,-1) through (106.91,-6.37,-98.9)mm
